# Revit family: Furniture_Chair_ECO 501P
name_source: partatom
category: Furniture
units: mm (PartAtom-declared; Revit-internal decimal feet)

## family parameters
Always vertical = No
Cut with Voids When Loaded = No
OmniClass Number = 23.21.23.15.17
Room Calculation Point = No
Shared = No
Work Plane-Based = Yes

## types (1)
- ECO 501P
    BIMobject category = Chair
    BIMobject category code = furniture-chair
    BIMobject main category = Furniture
    BIMobject main category code = furniture
    Brand url = https://www.sandlerseating.com
    Default Elevation = 0 mm  [stored 0 ft]
    Description = Chair
    Design country = Brasil
    Edition number = 1
    Frame Material = Wood - OAK - Natual OAK
    IFC Classification = Furnishing Element
    Manufacturer = Sandler
    Manufacturer country = USA
    Manufacturer name = Sandler
    Masterformat 2014 Code = 12 48 43.13
    Masterformat 2014 Description = Chair Mats
    Model = ECO 501P
    OmniClass Code = 23-21 23 15 17
    Product Guid = ??
    Product SKU = ??
    Product data url = https://www.sandlerseating.com
    Product family = Furniture
    Product group = Chair
    Product name = ECO 501P
    Product url = https://www.sandlerseating.com
    QR code = https://www.sandlerseating.com
    Shell Material = Leather - Positive AK019
    Uniformat II Description = Movable Furnishings

note: [stored X ft] marks values corroborated as IEEE doubles in the binary element streams (Revit-internal decimal feet)

## geometry (parser evidence)
native form markers: Blend x4, Sweep x5
no freeform markers — native parametric forms only
